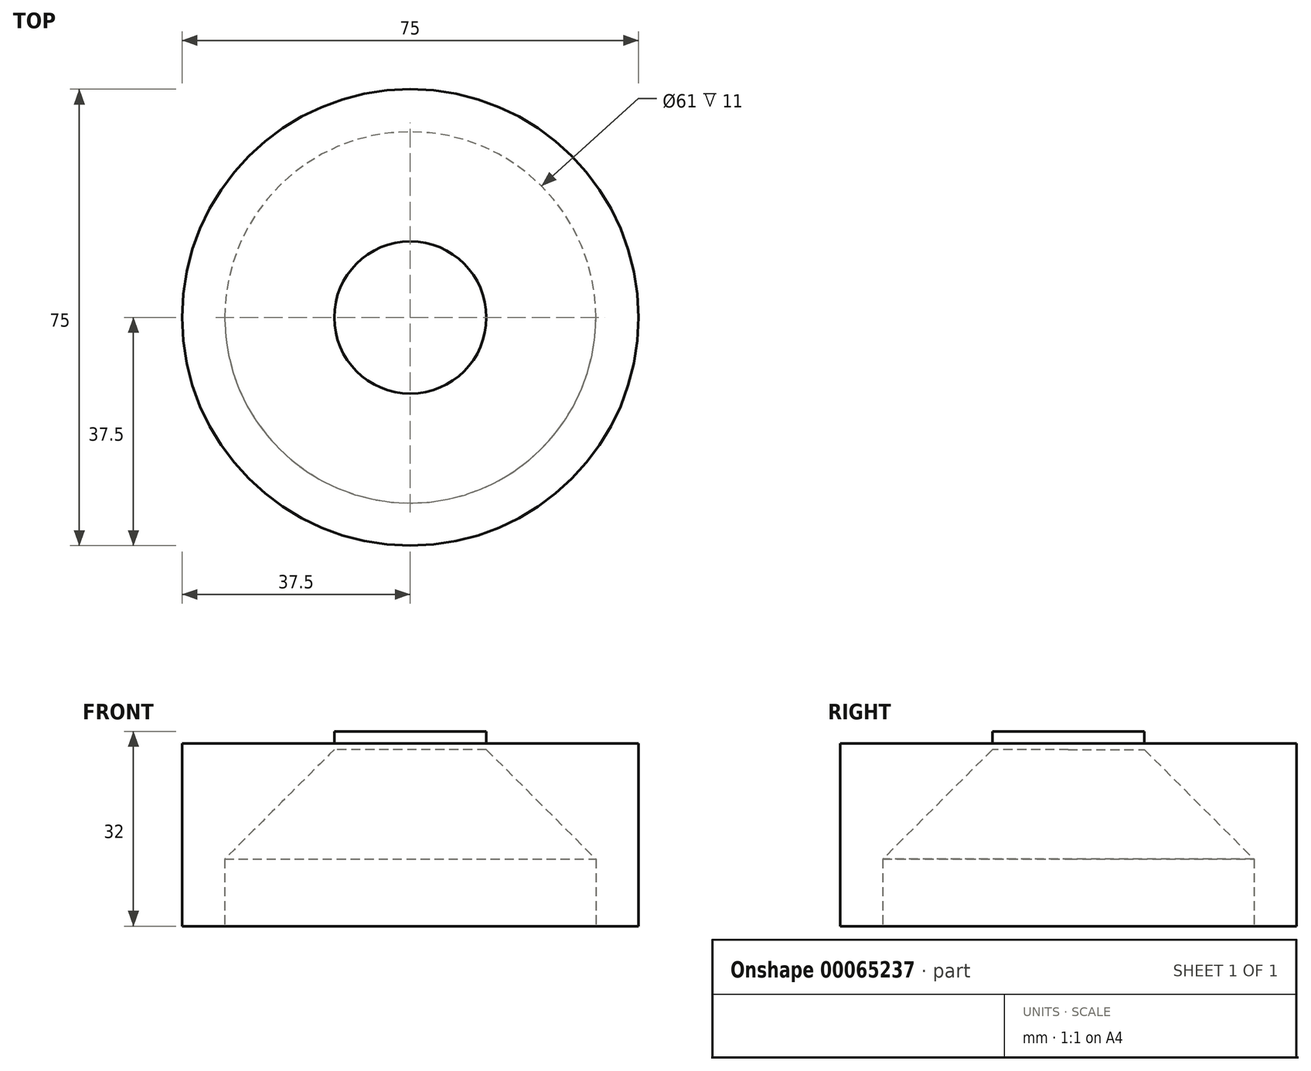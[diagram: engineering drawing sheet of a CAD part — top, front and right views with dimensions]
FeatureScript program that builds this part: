
annotation { "Feature Type Name" : "Feature", "Feature Type Description" : "" }
export const myFeature = defineFeature(function(context is Context, id is Id, definition is map)
    precondition{}
    {
        {
            var Q0;
            Q0=qCreatedBy(makeId("Top.planeOp"),FACE);
            var sketch = newSketch(context, id + "F0", { "sketchPlane" : qUnion([Q0])});
            skCircle(sketch, "E0", {"center": v(0, 0) * mm, "radius": 30.5 * mm});
            skCircle(sketch, "E1.0", {"center": v(0, 0) * mm, "radius": 37.5 * mm});
            skCircle(sketch, "E2", {"center": v(0, 0) * mm, "radius": 12.5 * mm});
            skSolve(sketch);
        }
        {
            var Q0;
            Q0=makeQuery(id+"F0.imprint","IMPRINT",FACE,{"disambiguationData":[TD([[makeQuery(id+"F0.imprint","IMPRINT",EDGE,{"derivedFrom":sQuery(id+"F0.wireOp",EDGE,"E0")}),-1.0]])]});
            extrude(context, id + "F1", {"entities" : qUnion([Q0]), "depth" : 40 * mm});
        }
        {
            var Q0;
            Q0=makeQuery(id+"F0.imprint","IMPRINT",FACE,{"disambiguationData":[TD([[makeQuery(id+"F0.imprint","IMPRINT",EDGE,{"derivedFrom":sQuery(id+"F0.wireOp",EDGE,"E0")}),1.0]])]});
            extrude(context, id + "F2", {"entities" : qUnion([Q0]), "operationType" : NewBodyOperationType.ADD, "depth" : 40 * mm, "hasSecondDirection" : true, "secondDirectionOppositeDirection" : false, "secondDirectionDepth" : 20 * mm});
        }
        {
            var Q0;
            Q0=makeQuery(id+"F0.imprint","IMPRINT",FACE,{"disambiguationData":[TD([[makeQuery(id+"F0.imprint","IMPRINT",EDGE,{"derivedFrom":sQuery(id+"F0.wireOp",EDGE,"E2")}),1.0]])]});
            extrude(context, id + "F3", {"entities" : qUnion([Q0]), "operationType" : NewBodyOperationType.ADD, "offsetDistance" : 25 * mm, "depth" : 42 * mm, "hasSecondDirection" : true, "secondDirectionOppositeDirection" : false, "secondDirectionDepth" : 39 * mm});
        }
        {
            var Q0;
            Q0=makeQuery(id+"F2.opExtrude","CAP_EDGE",EDGE,{"disambiguationData":[OSD([sQuery(id+"F0.wireOp",EDGE,"E2")])],"isStart":true});
            chamfer(context, id + "F4", {"entities" : qUnion([Q0]), "width" : 19 * mm, "tangentPropagation" : true});
        }
        {
            var Q0;
            Q0=makeQuery(id+"F1.opExtrude","CAP_FACE",FACE,{"disambiguationData":[OSD([sQuery(id+"F0.wireOp",EDGE,"E0"),sQuery(id+"F0.wireOp",EDGE,"E1.0")])],"isStart":true});
            extrude(context, id + "F5", {"entities" : qUnion([Q0]), "operationType" : NewBodyOperationType.REMOVE, "oppositeDirection" : true, "depth" : 10 * mm, "offsetDistance" : 25 * mm});
        }
    });
